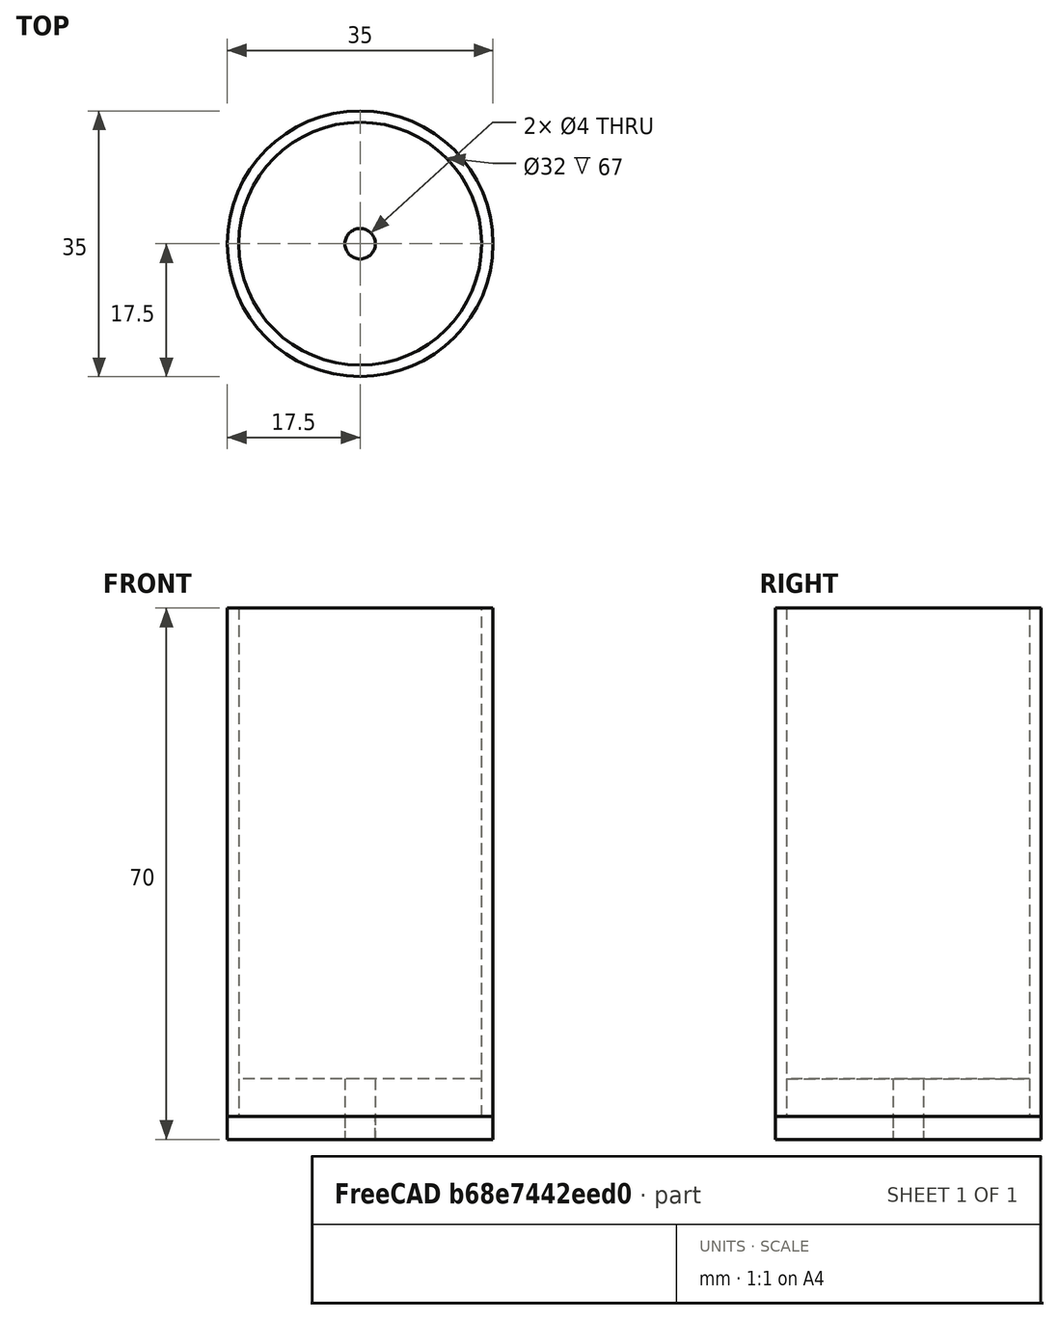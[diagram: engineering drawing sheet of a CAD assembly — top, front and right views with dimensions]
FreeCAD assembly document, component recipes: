
FREECAD ASSEMBLY — COMPONENT RECIPES ("tube")

This assembly document has 2 components, labeled P0..P1 below (a component is one placed body or linked part). 2 of them carry a construction recipe — the FreeCAD feature program that regenerates the part from scratch, quoted from this document or its linked companion documents; the rest are supplied as boundary geometry only. No exploded tour is included for this assembly.
COMPONENT P0 — recipe-attached ("case001", modeled in this document).
Construction recipe (the document's own serialized feature program — sketch geometry with constraints, then the solid features built on it; lengths are millimeters unless a unit is written):

FEATURE [Sketcher::SketchObject] Sketch
  ArcFitTolerance = 0
  AttachmentSupport = -> [XY_Plane]
  FullyConstrained = true
  MakeInternals = false
  MapMode = 5
  expr: Constraints[1] = <<parameters>>.outer_diameter
  expr: Constraints[3] = <<parameters>>.inner_diameter
  expr: Constraints[5] = <<parameters>>.hole_diameter
  sketch-geometry (3):
    g0: Circle CenterX=0 CenterY=0 CenterZ=0 NormalX=0 NormalY=0 NormalZ=1 AngleXU=0 Radius=17.5
    g1: Circle CenterX=0 CenterY=0 CenterZ=0 NormalX=0 NormalY=0 NormalZ=1 AngleXU=0 Radius=16
    g2: Circle CenterX=0 CenterY=0 CenterZ=0 NormalX=0 NormalY=0 NormalZ=1 AngleXU=0 Radius=2
  constraints (6):
    c: Coincident(g0,g-1)
    c: Diameter(g0) = 35
    c: Coincident(g1,g0)
    c: Diameter(g1) = 32
    c: Coincident(g2,g0)
    c: Diameter(g2) = 4
FEATURE [PartDesign::Pad] Pad  label="endcap"
  Direction = (0,0,1)
  Length = 3
  Length2 = 10
  Profile = -> Sketch [Edge3,Edge1]
  ReferenceAxis = -> Sketch [N_Axis]
  Refine = true
  Suppressed = false
  Type = 0
  expr: Length = <<parameters>>.cap_height
FEATURE [PartDesign::Pad] Pad001  label="walls"
  BaseFeature = -> Pad
  Direction = (0,0,1)
  Length = 70
  Length2 = 10
  Profile = -> Sketch [Edge1,Edge2]
  ReferenceAxis = -> Sketch [N_Axis]
  Refine = true
  Suppressed = false
  Type = 0
  expr: Length = <<parameters>>.total_length
FEATURE [PartDesign::Body] Body  label="case"
  AllowCompound = false
  Group = -> [Sketch,Pad,Pad001]
  Origin = -> Origin
  Tip = -> Pad001
COMPONENT P1 — recipe-attached ("lid001", modeled in this document).
Construction recipe (the document's own serialized feature program — sketch geometry with constraints, then the solid features built on it; lengths are millimeters unless a unit is written):

FEATURE [PartDesign::SubShapeBinder] Binder
  BindCopyOnChange = 0
  BindMode = 0
  ClaimChildren = false
  Context = -> Body001 [Binder.]
  Fuse = false
  MakeFace = true
  OffsetFill = false
  OffsetIntersection = false
  OffsetJoinType = 0
  OffsetOpenResult = false
  PartialLoad = false
  Refine = true
  Relative = true
  Support = -> [Body[Sketch.]]
  _Version = 2
FEATURE [PartDesign::Pad] Pad002  label="recess"
  Direction = (0,0,1)
  Length = 8
  Length2 = 10
  Profile = -> Binder [Edge3,Edge2]
  Refine = true
  Suppressed = false
  Type = 0
  expr: Length = <<parameters>>.cap_recess_height + <<parameters>>.cap_height
FEATURE [PartDesign::Pad] Pad003  label="lip"
  BaseFeature = -> Pad002
  Direction = (0,0,1)
  Length = 3
  Length2 = 10
  Profile = -> Binder [Edge1,Edge3]
  Refine = true
  Suppressed = false
  Type = 0
  expr: Length = <<parameters>>.cap_height
FEATURE [PartDesign::Body] Body001  label="lid"
  AllowCompound = false
  Group = -> [Binder,Pad002,Pad003]
  Origin = -> Origin001
  Tip = -> Pad003
PROVENANCE & LICENSES
A FreeCAD (.FCStd) document from a public repository crawl; recipes are the document's own serialized feature recipes (and, for linked parts, companion documents' recipes).
License: as declared in the source repository (recorded in the dataset sidecar).
